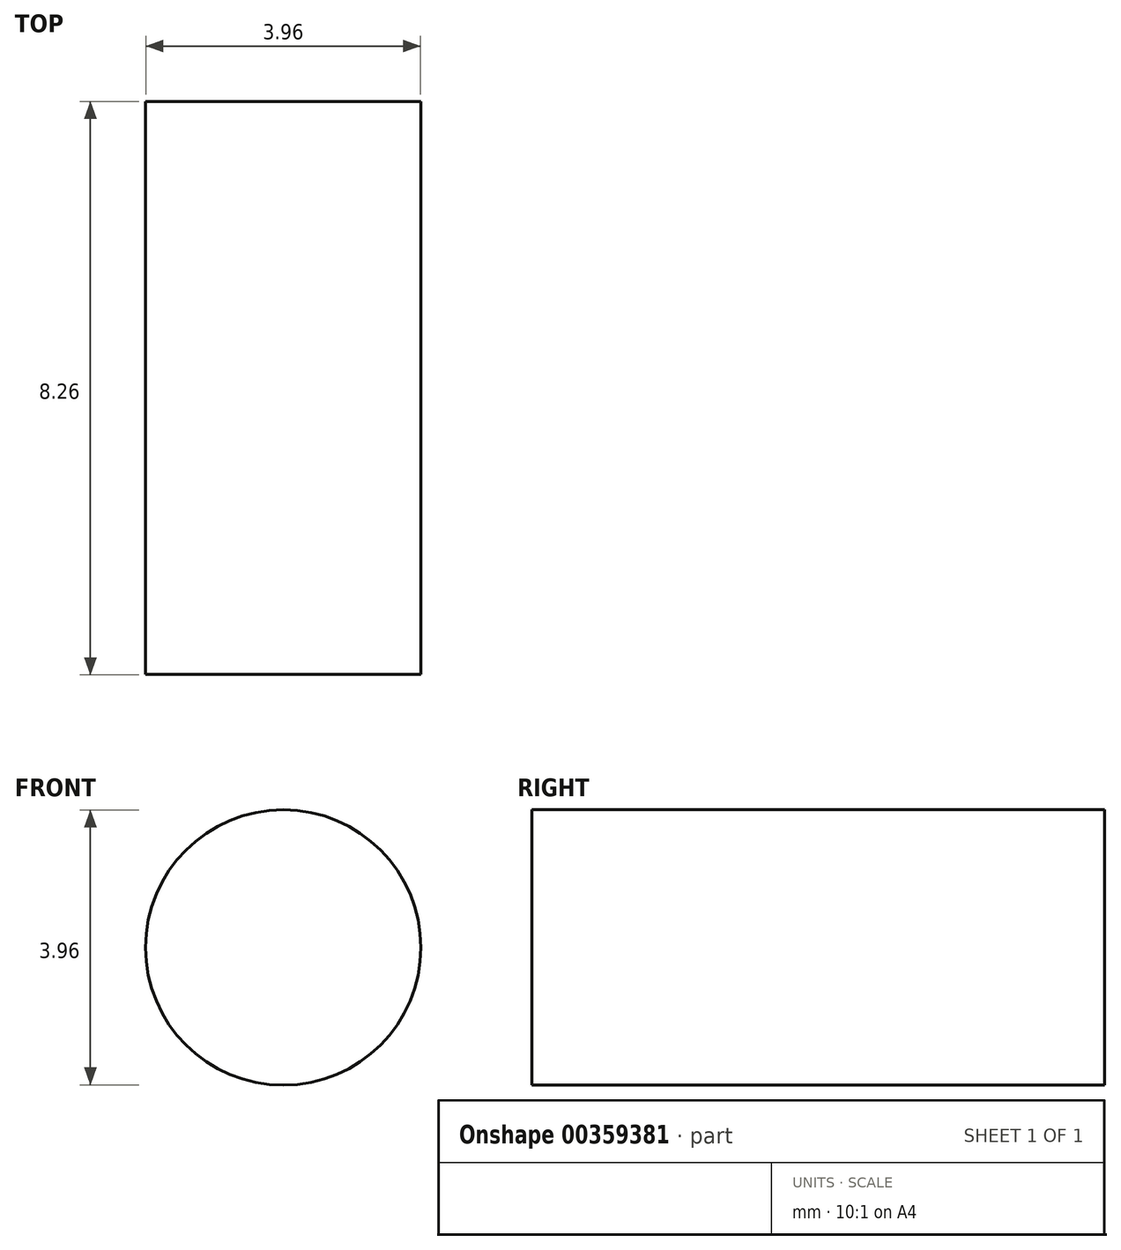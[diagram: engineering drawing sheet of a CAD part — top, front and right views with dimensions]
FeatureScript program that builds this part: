
annotation { "Feature Type Name" : "Feature", "Feature Type Description" : "" }
export const myFeature = defineFeature(function(context is Context, id is Id, definition is map)
    precondition{}
    {
        {
            var Q0;
            Q0=qCreatedBy(makeId("Front.planeOp"),FACE);
            var sketch = newSketch(context, id + "F0", { "sketchPlane" : qUnion([Q0])});
            skCircle(sketch, "E0", {"center": v(0, 0) * mm, "radius": 1.98 * mm});
            skSolve(sketch);
        }
        {
            var Q0;
            Q0=makeQuery(id+"F0.imprint","IMPRINT",FACE,{"disambiguationData":[TD([[makeQuery(id+"F0.imprint","IMPRINT",EDGE,{"derivedFrom":sQuery(id+"F0.wireOp",EDGE,"E0")}),1.0]])]});
            extrude(context, id + "F1", {"entities" : qUnion([Q0]), "depth" : 8.25 * mm});
        }
    });
